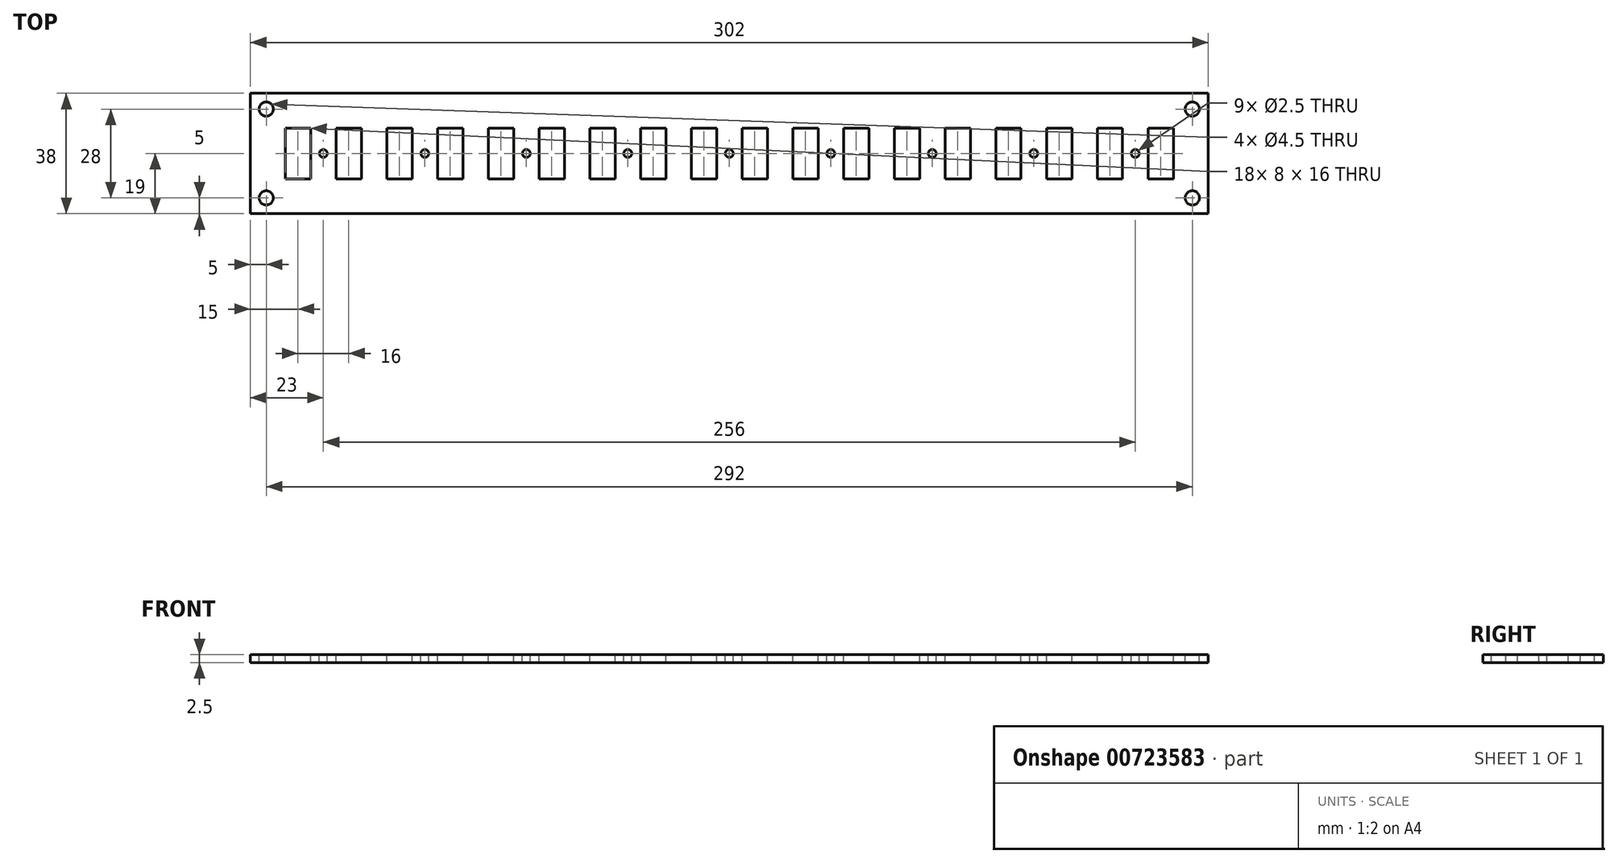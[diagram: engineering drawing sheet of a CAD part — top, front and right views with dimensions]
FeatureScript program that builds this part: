
annotation { "Feature Type Name" : "Feature", "Feature Type Description" : "" }
export const myFeature = defineFeature(function(context is Context, id is Id, definition is map)
    precondition{}
    {
        {
            var Q0;
            Q0=qCreatedBy(makeId("Top.planeOp"),FACE);
            var sketch = newSketch(context, id + "F0", { "sketchPlane" : qUnion([Q0])});
            skLineSegment(sketch, "E0.bottom", {"start": v(151, 19) * mm, "end": v(-151, 19) * mm});
            skLineSegment(sketch, "E0.top", {"start": v(151, -19) * mm, "end": v(-151, -19) * mm});
            skLineSegment(sketch, "E0.left", {"start": v(151, 19) * mm, "end": v(151, -19) * mm});
            skLineSegment(sketch, "E0.right", {"start": v(-151, 19) * mm, "end": v(-151, -19) * mm});
            skPoint(sketch, "E0.middle", {"position": v(0, 0) * mm});
            skLineSegment(sketch, "E1", {"start": v(-151, 0) * mm, "end": v(151, 0) * mm, "construction": true});
            skPoint(sketch, "E2", {"position": v(128, 0) * mm});
            skPoint(sketch, "E3", {"position": v(96, 0) * mm});
            skPoint(sketch, "E4", {"position": v(64, 0) * mm});
            skPoint(sketch, "E5", {"position": v(32, 0) * mm});
            skLineSegment(sketch, "E6", {"start": v(0, -19) * mm, "end": v(0, 19) * mm, "construction": true});
            skPoint(sketch, "E7.MirrorP", {"position": v(-32, 0) * mm});
            skPoint(sketch, "E8.MirrorP", {"position": v(-64, 0) * mm});
            skPoint(sketch, "E9.MirrorP", {"position": v(-96, 0) * mm});
            skPoint(sketch, "E10.MirrorP", {"position": v(-128, 0) * mm});
            skPoint(sketch, "E11", {"position": v(146, -14) * mm});
            skPoint(sketch, "E12.MirrorP", {"position": v(-146, -14) * mm});
            skPoint(sketch, "E13.MirrorP", {"position": v(146, 14) * mm});
            skPoint(sketch, "E14.MirrorP", {"position": v(-146, 14) * mm});
            skLineSegment(sketch, "E15", {"start": v(-151, 37.85) * mm, "end": v(-136, 37.85) * mm, "construction": true});
            skLineSegment(sketch, "E16", {"start": v(-136, 37.85) * mm, "end": v(-136, -40.42) * mm, "construction": true});
            skLineSegment(sketch, "E17.bottom", {"start": v(-132, 8) * mm, "end": v(-140, 8) * mm});
            skLineSegment(sketch, "E17.top", {"start": v(-132, -8) * mm, "end": v(-140, -8) * mm});
            skLineSegment(sketch, "E17.left", {"start": v(-132, 8) * mm, "end": v(-132, -8) * mm});
            skLineSegment(sketch, "E17.right", {"start": v(-140, 8) * mm, "end": v(-140, -8) * mm});
            skPoint(sketch, "E17.middle", {"position": v(-136, 0) * mm});
            skLineSegment(sketch, "E18.1.0.0", {"start": v(-116, 8) * mm, "end": v(-124, 8) * mm});
            skLineSegment(sketch, "E18.1.0.1", {"start": v(-116, 8) * mm, "end": v(-116, -8) * mm});
            skLineSegment(sketch, "E18.1.0.2", {"start": v(-124, 8) * mm, "end": v(-124, -8) * mm});
            skLineSegment(sketch, "E18.1.0.3", {"start": v(-116, -8) * mm, "end": v(-124, -8) * mm});
            skLineSegment(sketch, "E18.2.0.0", {"start": v(-100, 8) * mm, "end": v(-108, 8) * mm});
            skLineSegment(sketch, "E18.2.0.1", {"start": v(-100, 8) * mm, "end": v(-100, -8) * mm});
            skLineSegment(sketch, "E18.2.0.2", {"start": v(-108, 8) * mm, "end": v(-108, -8) * mm});
            skLineSegment(sketch, "E18.2.0.3", {"start": v(-100, -8) * mm, "end": v(-108, -8) * mm});
            skLineSegment(sketch, "E18.3.0.0", {"start": v(-84, 8) * mm, "end": v(-92, 8) * mm});
            skLineSegment(sketch, "E18.3.0.1", {"start": v(-84, 8) * mm, "end": v(-84, -8) * mm});
            skLineSegment(sketch, "E18.3.0.2", {"start": v(-92, 8) * mm, "end": v(-92, -8) * mm});
            skLineSegment(sketch, "E18.3.0.3", {"start": v(-84, -8) * mm, "end": v(-92, -8) * mm});
            skLineSegment(sketch, "E18.4.0.0", {"start": v(-68, 8) * mm, "end": v(-76, 8) * mm});
            skLineSegment(sketch, "E18.4.0.1", {"start": v(-68, 8) * mm, "end": v(-68, -8) * mm});
            skLineSegment(sketch, "E18.4.0.2", {"start": v(-76, 8) * mm, "end": v(-76, -8) * mm});
            skLineSegment(sketch, "E18.4.0.3", {"start": v(-68, -8) * mm, "end": v(-76, -8) * mm});
            skLineSegment(sketch, "E18.5.0.0", {"start": v(-52, 8) * mm, "end": v(-60, 8) * mm});
            skLineSegment(sketch, "E18.5.0.1", {"start": v(-52, 8) * mm, "end": v(-52, -8) * mm});
            skLineSegment(sketch, "E18.5.0.2", {"start": v(-60, 8) * mm, "end": v(-60, -8) * mm});
            skLineSegment(sketch, "E18.5.0.3", {"start": v(-52, -8) * mm, "end": v(-60, -8) * mm});
            skLineSegment(sketch, "E18.6.0.0", {"start": v(-36, 8) * mm, "end": v(-44, 8) * mm});
            skLineSegment(sketch, "E18.6.0.1", {"start": v(-36, 8) * mm, "end": v(-36, -8) * mm});
            skLineSegment(sketch, "E18.6.0.2", {"start": v(-44, 8) * mm, "end": v(-44, -8) * mm});
            skLineSegment(sketch, "E18.6.0.3", {"start": v(-36, -8) * mm, "end": v(-44, -8) * mm});
            skLineSegment(sketch, "E18.7.0.0", {"start": v(-20, 8) * mm, "end": v(-28, 8) * mm});
            skLineSegment(sketch, "E18.7.0.1", {"start": v(-20, 8) * mm, "end": v(-20, -8) * mm});
            skLineSegment(sketch, "E18.7.0.2", {"start": v(-28, 8) * mm, "end": v(-28, -8) * mm});
            skLineSegment(sketch, "E18.7.0.3", {"start": v(-20, -8) * mm, "end": v(-28, -8) * mm});
            skLineSegment(sketch, "E18.8.0.0", {"start": v(-4, 8) * mm, "end": v(-12, 8) * mm});
            skLineSegment(sketch, "E18.8.0.1", {"start": v(-4, 8) * mm, "end": v(-4, -8) * mm});
            skLineSegment(sketch, "E18.8.0.2", {"start": v(-12, 8) * mm, "end": v(-12, -8) * mm});
            skLineSegment(sketch, "E18.8.0.3", {"start": v(-4, -8) * mm, "end": v(-12, -8) * mm});
            skLineSegment(sketch, "E18.9.0.0", {"start": v(12, 8) * mm, "end": v(4, 8) * mm});
            skLineSegment(sketch, "E18.9.0.1", {"start": v(12, 8) * mm, "end": v(12, -8) * mm});
            skLineSegment(sketch, "E18.9.0.2", {"start": v(4, 8) * mm, "end": v(4, -8) * mm});
            skLineSegment(sketch, "E18.9.0.3", {"start": v(12, -8) * mm, "end": v(4, -8) * mm});
            skLineSegment(sketch, "E18.10.0.0", {"start": v(28, 8) * mm, "end": v(20, 8) * mm});
            skLineSegment(sketch, "E18.10.0.1", {"start": v(28, 8) * mm, "end": v(28, -8) * mm});
            skLineSegment(sketch, "E18.10.0.2", {"start": v(20, 8) * mm, "end": v(20, -8) * mm});
            skLineSegment(sketch, "E18.10.0.3", {"start": v(28, -8) * mm, "end": v(20, -8) * mm});
            skLineSegment(sketch, "E18.11.0.0", {"start": v(44, 8) * mm, "end": v(36, 8) * mm});
            skLineSegment(sketch, "E18.11.0.1", {"start": v(44, 8) * mm, "end": v(44, -8) * mm});
            skLineSegment(sketch, "E18.11.0.2", {"start": v(36, 8) * mm, "end": v(36, -8) * mm});
            skLineSegment(sketch, "E18.11.0.3", {"start": v(44, -8) * mm, "end": v(36, -8) * mm});
            skLineSegment(sketch, "E18.12.0.0", {"start": v(60, 8) * mm, "end": v(52, 8) * mm});
            skLineSegment(sketch, "E18.12.0.1", {"start": v(60, 8) * mm, "end": v(60, -8) * mm});
            skLineSegment(sketch, "E18.12.0.2", {"start": v(52, 8) * mm, "end": v(52, -8) * mm});
            skLineSegment(sketch, "E18.12.0.3", {"start": v(60, -8) * mm, "end": v(52, -8) * mm});
            skLineSegment(sketch, "E18.13.0.0", {"start": v(76, 8) * mm, "end": v(68, 8) * mm});
            skLineSegment(sketch, "E18.13.0.1", {"start": v(76, 8) * mm, "end": v(76, -8) * mm});
            skLineSegment(sketch, "E18.13.0.2", {"start": v(68, 8) * mm, "end": v(68, -8) * mm});
            skLineSegment(sketch, "E18.13.0.3", {"start": v(76, -8) * mm, "end": v(68, -8) * mm});
            skLineSegment(sketch, "E18.14.0.0", {"start": v(92, 8) * mm, "end": v(84, 8) * mm});
            skLineSegment(sketch, "E18.14.0.1", {"start": v(92, 8) * mm, "end": v(92, -8) * mm});
            skLineSegment(sketch, "E18.14.0.2", {"start": v(84, 8) * mm, "end": v(84, -8) * mm});
            skLineSegment(sketch, "E18.14.0.3", {"start": v(92, -8) * mm, "end": v(84, -8) * mm});
            skLineSegment(sketch, "E18.15.0.0", {"start": v(108, 8) * mm, "end": v(100, 8) * mm});
            skLineSegment(sketch, "E18.15.0.1", {"start": v(108, 8) * mm, "end": v(108, -8) * mm});
            skLineSegment(sketch, "E18.15.0.2", {"start": v(100, 8) * mm, "end": v(100, -8) * mm});
            skLineSegment(sketch, "E18.15.0.3", {"start": v(108, -8) * mm, "end": v(100, -8) * mm});
            skLineSegment(sketch, "E18.16.0.0", {"start": v(124, 8) * mm, "end": v(116, 8) * mm});
            skLineSegment(sketch, "E18.16.0.1", {"start": v(124, 8) * mm, "end": v(124, -8) * mm});
            skLineSegment(sketch, "E18.16.0.2", {"start": v(116, 8) * mm, "end": v(116, -8) * mm});
            skLineSegment(sketch, "E18.16.0.3", {"start": v(124, -8) * mm, "end": v(116, -8) * mm});
            skLineSegment(sketch, "E18.17.0.0", {"start": v(140, 8) * mm, "end": v(132, 8) * mm});
            skLineSegment(sketch, "E18.17.0.1", {"start": v(140, 8) * mm, "end": v(140, -8) * mm});
            skLineSegment(sketch, "E18.17.0.2", {"start": v(132, 8) * mm, "end": v(132, -8) * mm});
            skLineSegment(sketch, "E18.17.0.3", {"start": v(140, -8) * mm, "end": v(132, -8) * mm});
            skLineSegment(sketch, "E18.direction1", {"start": v(-140, -8) * mm, "end": v(-124, -8) * mm, "construction": true});
            skSolve(sketch);
        }
        {
            var Q0;
            Q0=makeQuery(id+"F0.imprint","IMPRINT",FACE,{"disambiguationData":[TD([[makeQuery(id+"F0.imprint","IMPRINT",EDGE,{"derivedFrom":sQuery(id+"F0.wireOp",EDGE,"E0.bottom")}),1.0]])]});
            extrude(context, id + "F1", {"entities" : qUnion([Q0]), "oppositeDirection" : true, "depth" : 2.5 * mm, "offsetDistance" : 25 * mm});
        }
        {
            var Q0;
            Q0=sQuery(id+"F0.wireOp",VERTEX,"E10.MirrorP");
            var Q1;
            Q1=sQuery(id+"F0.wireOp",VERTEX,"E9.MirrorP");
            var Q2;
            Q2=sQuery(id+"F0.wireOp",VERTEX,"E8.MirrorP");
            var Q3;
            Q3=sQuery(id+"F0.wireOp",VERTEX,"E7.MirrorP");
            var Q4;
            Q4=sQuery(id+"F0.wireOp",VERTEX,"E0.middle");
            var Q5;
            Q5=sQuery(id+"F0.wireOp",VERTEX,"E5");
            var Q6;
            Q6=sQuery(id+"F0.wireOp",VERTEX,"E4");
            var Q7;
            Q7=sQuery(id+"F0.wireOp",VERTEX,"E3");
            var Q8;
            Q8=sQuery(id+"F0.wireOp",VERTEX,"E2");
            var Q9;
            Q9=makeQuery(id+"F1.opExtrude","SWEPT_BODY",BODY,{"disambiguationData":[OSD([sQuery(id+"F0.wireOp",EDGE,"E0.bottom"),sQuery(id+"F0.wireOp",EDGE,"E0.top"),sQuery(id+"F0.wireOp",EDGE,"E0.left"),sQuery(id+"F0.wireOp",EDGE,"E0.right")])]});
            hole(context, id + "F2", {"style" : HoleStyle.SIMPLE, "endStyle" : HoleEndStyle.THROUGH, "holeDiameter" : 2.5 * mm, "majorDiameter" : 5 * mm, "isTappedThrough" : true, "tappedDepth" : 12 * mm, "tapClearance" : 3, "startFromSketch" : true, "locations" : qUnion([Q0, Q1, Q2, Q3, Q4, Q5, Q6, Q7, Q8]), "scope" : qUnion([Q9])});
        }
        {
            var Q0;
            Q0=sQuery(id+"F0.wireOp",VERTEX,"E14.MirrorP");
            var Q1;
            Q1=sQuery(id+"F0.wireOp",VERTEX,"E12.MirrorP");
            var Q2;
            Q2=sQuery(id+"F0.wireOp",VERTEX,"E13.MirrorP");
            var Q3;
            Q3=sQuery(id+"F0.wireOp",VERTEX,"E11");
            var Q4;
            Q4=makeQuery(id+"F1.opExtrude","SWEPT_BODY",BODY,{"disambiguationData":[OSD([sQuery(id+"F0.wireOp",EDGE,"E0.bottom"),sQuery(id+"F0.wireOp",EDGE,"E0.top"),sQuery(id+"F0.wireOp",EDGE,"E0.left"),sQuery(id+"F0.wireOp",EDGE,"E0.right")])]});
            hole(context, id + "F3", {"style" : HoleStyle.SIMPLE, "endStyle" : HoleEndStyle.THROUGH, "holeDiameter" : 4.5 * mm, "majorDiameter" : 5 * mm, "isTappedThrough" : true, "tappedDepth" : 12 * mm, "tapClearance" : 3, "startFromSketch" : true, "locations" : qUnion([Q0, Q1, Q2, Q3]), "scope" : qUnion([Q4])});
        }
        {
            var Q0;
            Q0=makeQuery(id+"F0.imprint","IMPRINT",FACE,{"disambiguationData":[TD([[makeQuery(id+"F0.imprint","IMPRINT",EDGE,{"derivedFrom":sQuery(id+"F0.wireOp",EDGE,"E17.bottom")}),1.0]])]});
            extrude(context, id + "F4", {"entities" : qUnion([Q0]), "operationType" : NewBodyOperationType.REMOVE, "endBound" : BoundingType.THROUGH_ALL, "oppositeDirection" : true, "depth" : 25 * mm, "offsetDistance" : 25 * mm});
        }
    });
